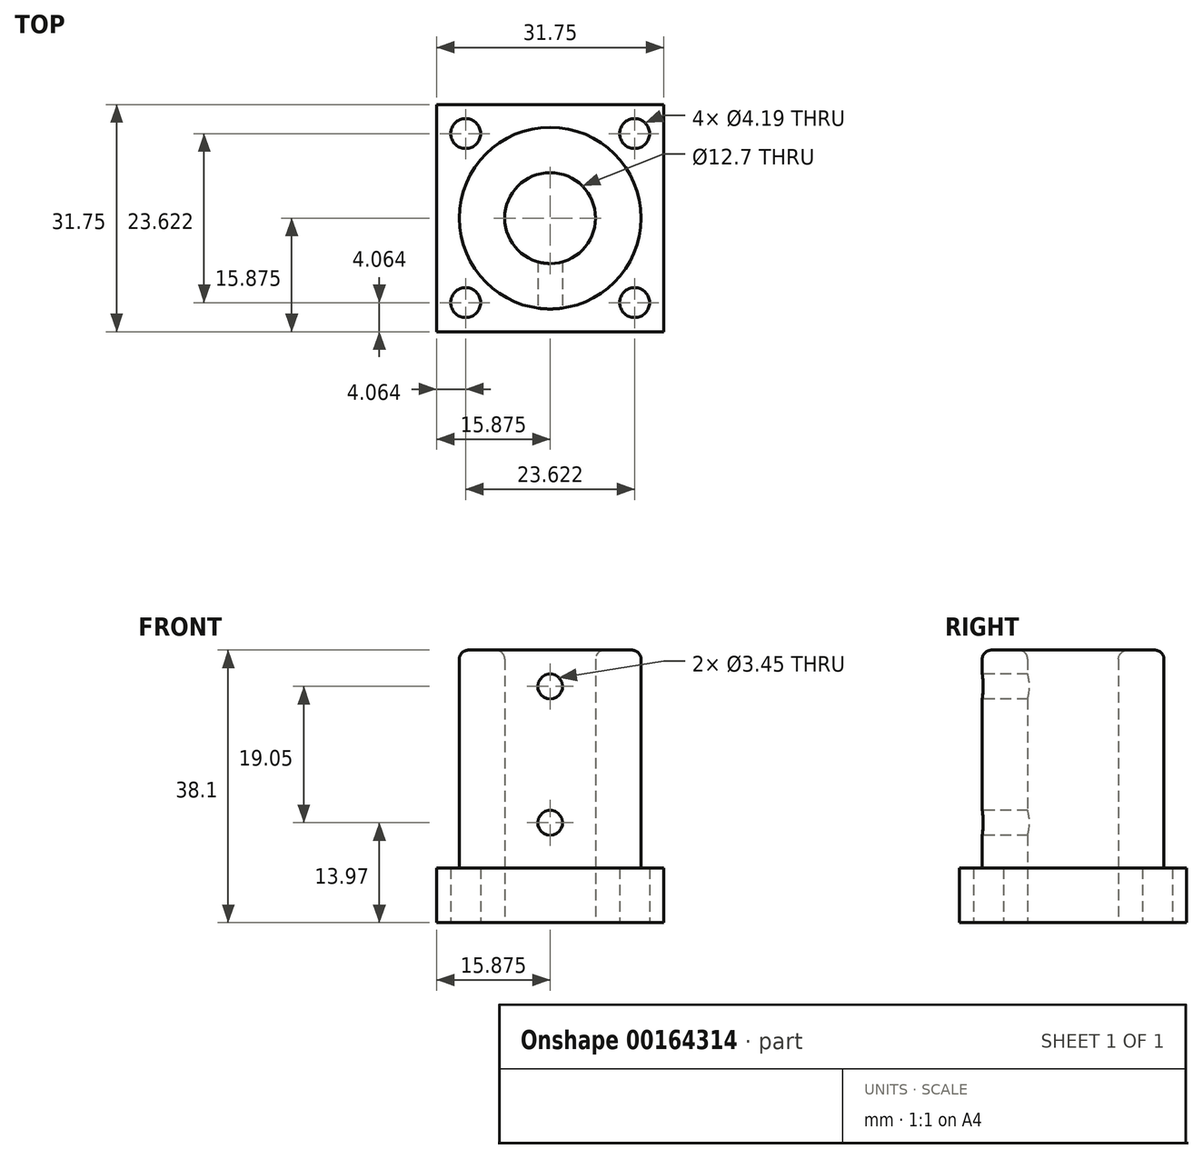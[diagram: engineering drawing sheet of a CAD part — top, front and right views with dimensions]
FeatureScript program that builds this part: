
annotation { "Feature Type Name" : "Feature", "Feature Type Description" : "" }
export const myFeature = defineFeature(function(context is Context, id is Id, definition is map)
    precondition{}
    {
        {
            var Q0;
            Q0=qCreatedBy(makeId("Top.planeOp"),FACE);
            var sketch = newSketch(context, id + "F0", { "sketchPlane" : qUnion([Q0])});
            skLineSegment(sketch, "E0.bottom", {"start": v(0, 0) * mm, "end": v(31.75, 0) * mm});
            skLineSegment(sketch, "E0.top", {"start": v(0, 31.75) * mm, "end": v(31.75, 31.75) * mm});
            skLineSegment(sketch, "E0.left", {"start": v(0, 0) * mm, "end": v(0, 31.75) * mm});
            skLineSegment(sketch, "E0.right", {"start": v(31.75, 0) * mm, "end": v(31.75, 31.75) * mm});
            skLineSegment(sketch, "E1", {"start": v(0, 31.75) * mm, "end": v(31.75, 0) * mm, "construction": true});
            skCircle(sketch, "E2", {"center": v(15.87, 15.88) * mm, "radius": 12.7 * mm});
            skCircle(sketch, "E3", {"center": v(4.06, 27.69) * mm, "radius": 2.1 * mm});
            skCircle(sketch, "E4", {"center": v(27.69, 4.06) * mm, "radius": 2.1 * mm});
            skLineSegment(sketch, "E5", {"start": v(0, 0) * mm, "end": v(31.75, 31.75) * mm, "construction": true});
            skCircle(sketch, "E6", {"center": v(27.69, 27.69) * mm, "radius": 2.1 * mm});
            skCircle(sketch, "E7", {"center": v(4.06, 4.06) * mm, "radius": 2.1 * mm});
            skCircle(sketch, "E8", {"center": v(15.87, 15.88) * mm, "radius": 6.35 * mm});
            skSolve(sketch);
        }
        {
            var Q0;
            Q0 = qSketchRegion(id + "F0", true);
            extrude(context, id + "F1", {"entities" : qUnion([Q0]), "depth" : 7.62 * mm});
        }
        {
            var Q0;
            Q0=makeQuery(id+"F0.imprint","IMPRINT",FACE,{"disambiguationData":[TD([[makeQuery(id+"F0.imprint","IMPRINT",EDGE,{"derivedFrom":sQuery(id+"F0.wireOp",EDGE,"E2")}),1.0]])]});
            extrude(context, id + "F2", {"entities" : qUnion([Q0]), "operationType" : NewBodyOperationType.ADD, "depth" : 38.1 * mm});
        }
        {
            var Q0;
            Q0=qCreatedBy(makeId("Front.planeOp"),FACE);
            var sketch = newSketch(context, id + "F3", { "sketchPlane" : qUnion([Q0])});
            skCircle(sketch, "E9", {"center": v(15.88, 13.97) * mm, "radius": 1.73 * mm});
            skCircle(sketch, "E10", {"center": v(15.88, 33.02) * mm, "radius": 1.73 * mm});
            skSolve(sketch);
        }
        {
            var Q0;
            Q0 = qSketchRegion(id + "F3", true);
            extrude(context, id + "F4", {"entities" : qUnion([Q0]), "operationType" : NewBodyOperationType.REMOVE, "oppositeDirection" : true, "depth" : 15.88 * mm});
        }
        {
            var Q0;
            Q0=makeQuery(id+"F2.opExtrude","CAP_EDGE",EDGE,{"disambiguationData":[OSD([sQuery(id+"F0.wireOp",EDGE,"E2")])],"isStart":false});
            var Q1;
            Q1=makeQuery(id+"F2.opExtrude","CAP_EDGE",EDGE,{"disambiguationData":[OSD([sQuery(id+"F0.wireOp",EDGE,"E8")])],"isStart":false});
            fillet(context, id + "F5", {"entities" : qUnion([Q0, Q1]), "radius" : 1.27 * mm, "tangentPropagation" : true, "allowEdgeOverflow" : false});
        }
    });
